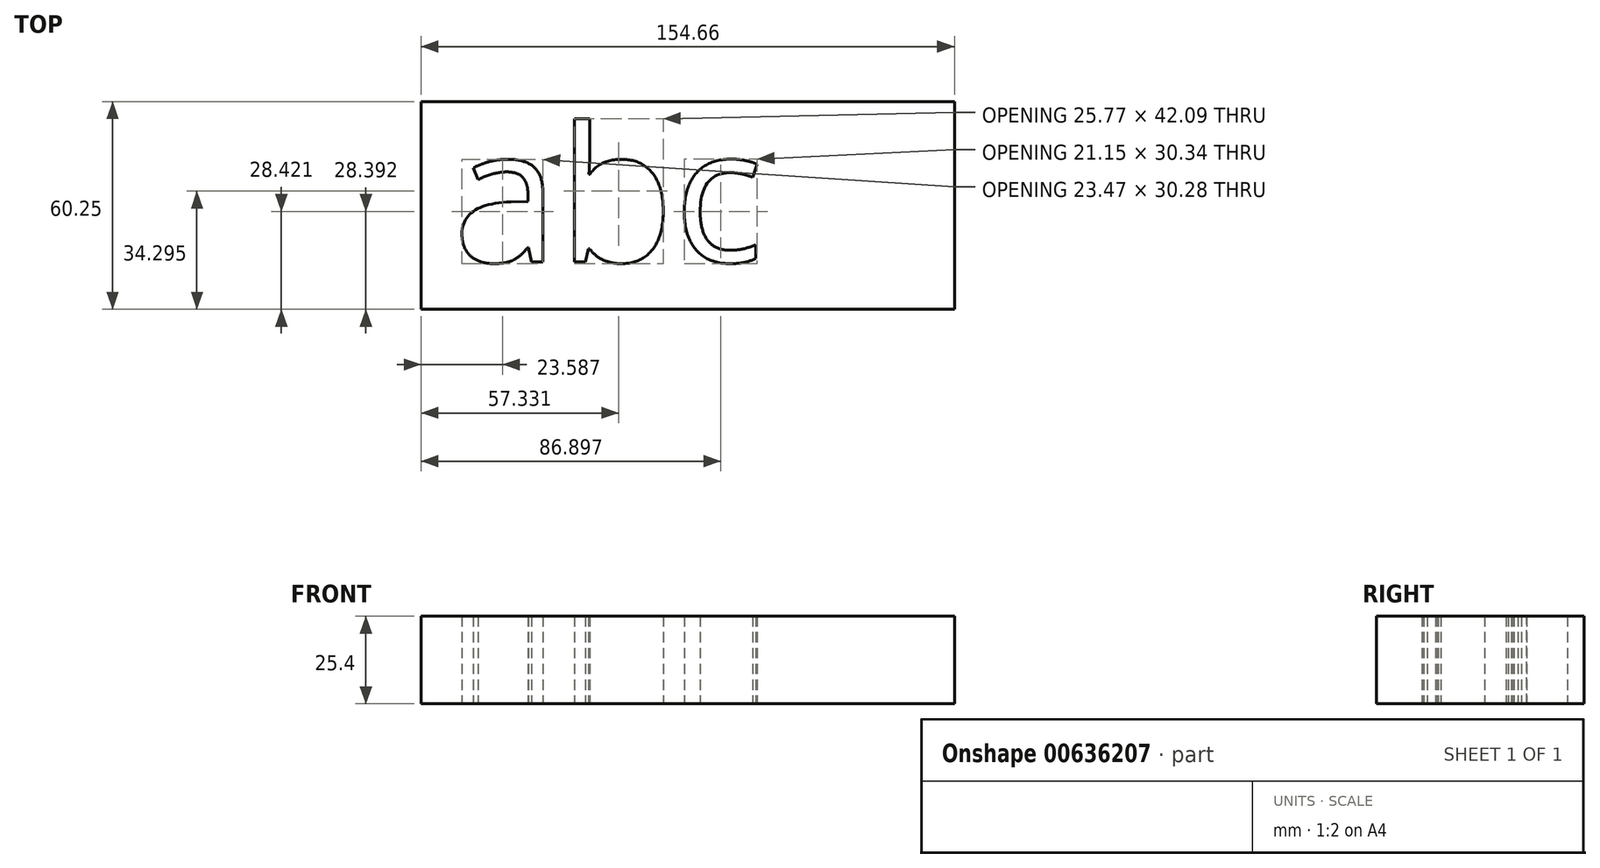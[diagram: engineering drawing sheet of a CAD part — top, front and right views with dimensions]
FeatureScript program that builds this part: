
annotation { "Feature Type Name" : "Feature", "Feature Type Description" : "" }
export const myFeature = defineFeature(function(context is Context, id is Id, definition is map)
    precondition{}
    {
        {
            var Q0;
            Q0=qCreatedBy(makeId("Top.planeOp"),FACE);
            var sketch = newSketch(context, id + "F0", { "sketchPlane" : qUnion([Q0])});
            skLineSegment(sketch, "E0.bottom", {"start": v(-79.24, 74.9) * mm, "end": v(75.42, 74.9) * mm});
            skLineSegment(sketch, "E0.top", {"start": v(-79.24, 14.66) * mm, "end": v(75.42, 14.66) * mm});
            skLineSegment(sketch, "E0.left", {"start": v(-79.24, 74.9) * mm, "end": v(-79.24, 14.66) * mm});
            skLineSegment(sketch, "E0.right", {"start": v(75.42, 74.9) * mm, "end": v(75.42, 14.66) * mm});
            skSolve(sketch);
        }
        {
            var Q0;
            Q0=makeQuery(id+"F0.imprint","IMPRINT",FACE,{"disambiguationData":[TD([[makeQuery(id+"F0.imprint","IMPRINT",EDGE,{"derivedFrom":sQuery(id+"F0.wireOp",EDGE,"E0.bottom")}),-1.0]])]});
            var sketch = newSketch(context, id + "F1", { "sketchPlane" : qUnion([Q0])});
            skText(sketch, "E1", { "text": "abc", "fontName": "OpenSans-Regular.ttf"});
            const initialGuessF1  = {"E1": [-0.0699, 0.02845, 1, 0, 0.03937]};
            skSetInitialGuess(sketch, initialGuessF1);
            skSolve(sketch);
        }
        {
            var Q0;
            Q0=makeQuery(id+"F1.imprint","IMPRINT",FACE,{"disambiguationData":[TD([[makeQuery(id+"F1.imprint","IMPRINT",EDGE,{"derivedFrom":sQuery(id+"F1.wireOp",EDGE,"E1.sketch_text.stroke-0")}),1.0]])]});
            extrude(context, id + "F2", {"entities" : qUnion([Q0]), "depth" : 25.4 * mm, "offsetDistance" : 25.4 * mm});
        }
    });
